# Revit family: F141-67X32.5X35
name_source: partatom
category: Furniture Systems
units: mm (PartAtom-declared; Revit-internal decimal feet)

## family parameters
Always vertical = Yes
Cut with Voids When Loaded = No
Part Type = Normal
Room Calculation Point = No
Round Connector Dimension = Use Diameter
Shared = No
Work Plane-Based = No

## types (9) — shared parameters
3" Rectangle Leg = <By Category>
6" Rectangle Leg = <By Category>
Back Fabric = <By Category>
Base = <By Category>
Caster = Default New Material(1)
Description = Linear Refresh - Linear Refresh Sofa (Seat height 18")
Glide = <By Category>
Low Profile = Black
Manufacturer = FOMCORE
Mod Leg = <By Category>
Model = F141-67X32.5X35
Seat Fabric = <By Category>
Sled Leg = <By Category>
Sled Leg 29 = <By Category>
Triangle Leg = <By Category>
URL = https://fomcore.com

## per-type parameters (varying)
| type | Base D1 | Base D2 | C3 | C6 | G1 | L1 | LEG OPTIONS | Leg H | M6 | R3 | R6 | S29 | Seat D | T6 |
| F141-67X32.5X35-C3 | 1' - 1 5/8" | 1' - 4 1/8" | Yes | No | No | No | 1 | 0' - 3 1/2" | No | No | No | No | 1' - 7 7/32" | No |
| F141-67X32.5X35-C6 | 1' - 2 13/32" | 1' - 3 27/32" | No | Yes | No | No | 2 | 0' - 6 1/2" | No | No | No | No | 1' - 8" | No |
| F141-67X32.5X35-G1 | 1' - 1 5/8" | 1' - 4 1/8" | No | No | Yes | No | 3 | 0' - 1 1/2" | No | No | No | No | 1' - 7 7/32" | No |
| F141-67X32.5X35-L1 | 1' - 1 5/8" | 1' - 4 1/8" | No | No | No | Yes | 4 | 0' - 1 1/2" | No | No | No | No | 1' - 7 7/32" | No |
| F141-67X32.5X35-M6 | 1' - 2 13/32" | 1' - 3 27/32" | No | No | No | No | 5 | 0' - 6 1/2" | Yes | No | No | No | 1' - 8" | No |
| F141-67X32.5X35-R3 | 1' - 1 5/8" | 1' - 4 1/8" | No | No | No | No | 6 | 0' - 3 1/2" | No | Yes | No | No | 1' - 7 7/32" | No |
| F141-67X32.5X35-R6 | 1' - 2 13/32" | 1' - 3 27/32" | No | No | No | No | 7 | 0' - 6 1/2" | No | No | Yes | No | 1' - 8" | No |
| F141-67X32.5X35-T6 | 1' - 2 13/32" | 1' - 3 27/32" | No | No | No | No | 9 | 0' - 6 1/2" | No | No | No | No | 1' - 8" | Yes |
| F141-67X32.5X35-S29 | 1' - 2 13/32" | 1' - 3 27/32" | No | No | No | No | 8 | 0' - 6 1/2" | No | No | No | Yes | 1' - 8" | No |

## geometry (parser evidence)
native form markers: Sweep x3
no freeform markers — native parametric forms only
